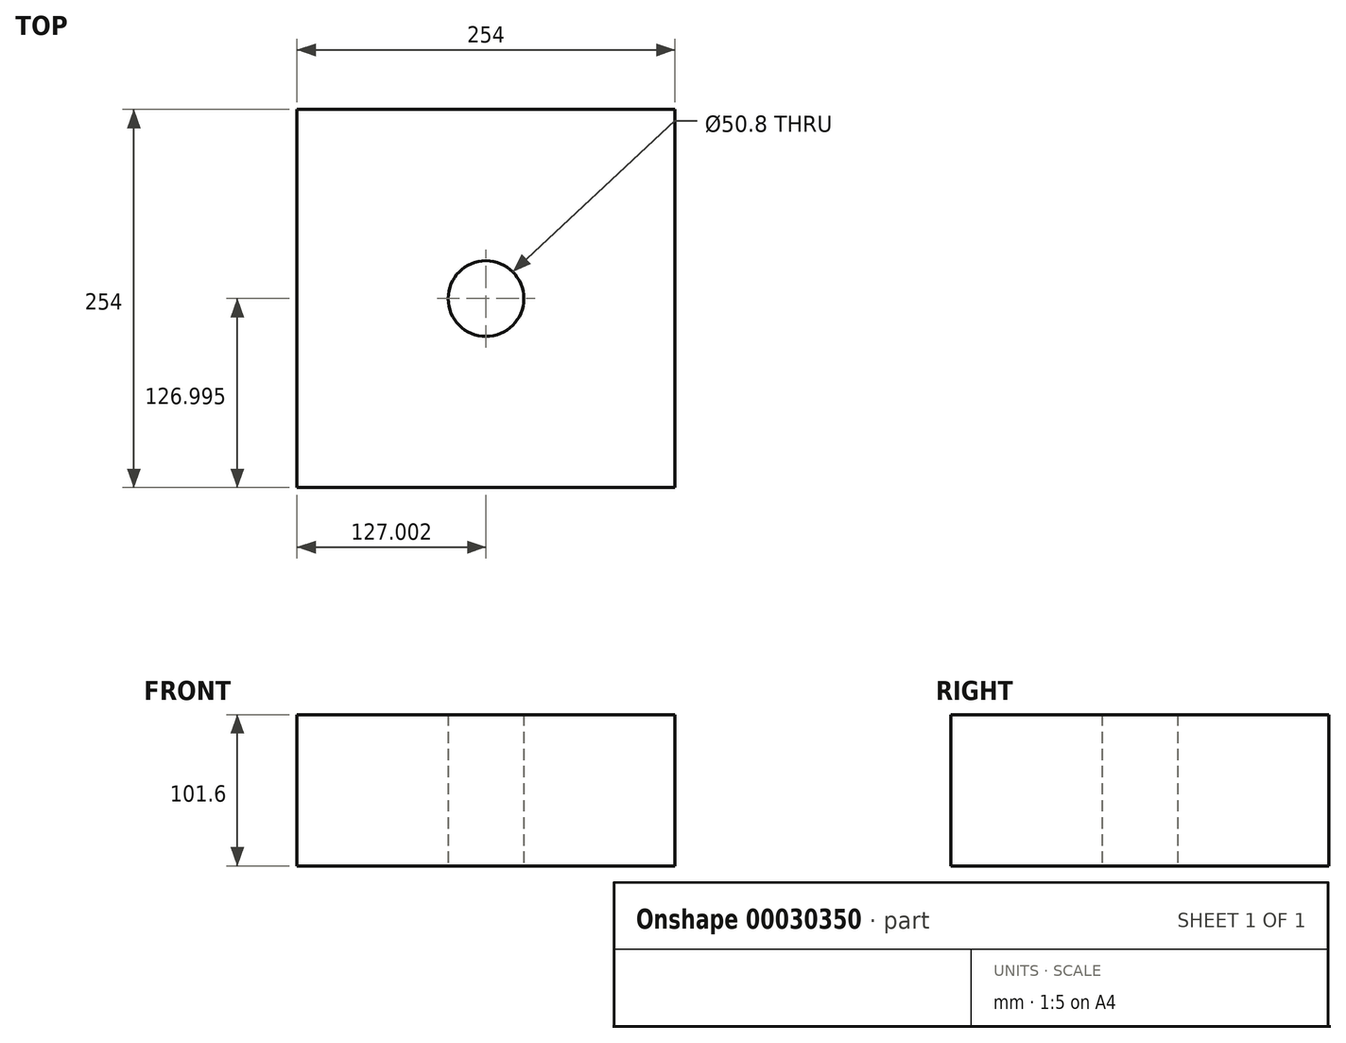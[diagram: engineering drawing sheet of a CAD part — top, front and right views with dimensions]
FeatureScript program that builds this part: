
annotation { "Feature Type Name" : "Feature", "Feature Type Description" : "" }
export const myFeature = defineFeature(function(context is Context, id is Id, definition is map)
    precondition{}
    {
        {
            var Q0;
            Q0=qCreatedBy(makeId("Top.planeOp"),FACE);
            var sketch = newSketch(context, id + "F0", { "sketchPlane" : qUnion([Q0])});
            skLineSegment(sketch, "E0.bottom", {"start": v(-114.49, 104.9) * mm, "end": v(139.51, 104.9) * mm});
            skLineSegment(sketch, "E0.top", {"start": v(-114.49, -149.1) * mm, "end": v(139.51, -149.1) * mm});
            skLineSegment(sketch, "E0.left", {"start": v(-114.49, 104.9) * mm, "end": v(-114.49, -149.1) * mm});
            skLineSegment(sketch, "E0.right", {"start": v(139.51, 104.9) * mm, "end": v(139.51, -149.1) * mm});
            skCircle(sketch, "E1", {"center": v(12.51, -22.1) * mm, "radius": 25.4 * mm});
            skSolve(sketch);
        }
        {
            var Q0;
            Q0 = qSketchRegion(id + "F0", true);
            extrude(context, id + "F1", {"entities" : qUnion([Q0]), "depth" : 101.6 * mm});
        }
    });
